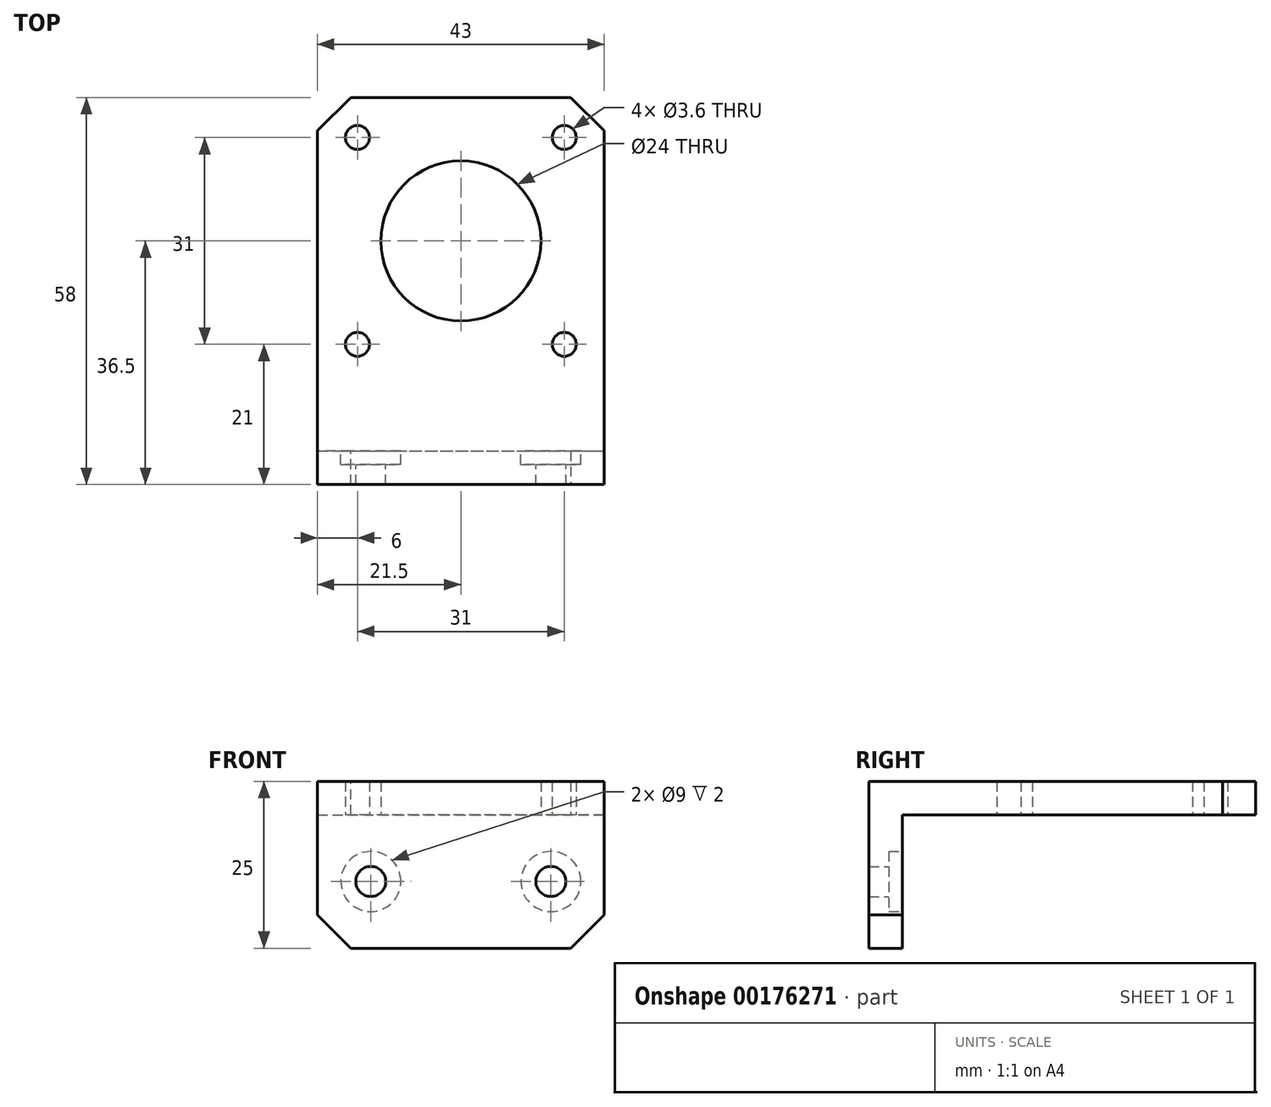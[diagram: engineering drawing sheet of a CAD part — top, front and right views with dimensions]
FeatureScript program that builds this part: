
annotation { "Feature Type Name" : "Feature", "Feature Type Description" : "" }
export const myFeature = defineFeature(function(context is Context, id is Id, definition is map)
    precondition{}
    {
        {
            var Q0;
            Q0=qCreatedBy(makeId("Top.planeOp"),FACE);
            var sketch = newSketch(context, id + "F0", { "sketchPlane" : qUnion([Q0])});
            skCircle(sketch, "E0", {"center": v(0, 0) * mm, "radius": 12 * mm});
            skLineSegment(sketch, "E1.bottom", {"start": v(15.5, -15.5) * mm, "end": v(-15.5, -15.5) * mm, "construction": true});
            skLineSegment(sketch, "E1.top", {"start": v(15.5, 15.5) * mm, "end": v(-15.5, 15.5) * mm, "construction": true});
            skLineSegment(sketch, "E1.left", {"start": v(15.5, -15.5) * mm, "end": v(15.5, 15.5) * mm, "construction": true});
            skLineSegment(sketch, "E1.right", {"start": v(-15.5, -15.5) * mm, "end": v(-15.5, 15.5) * mm, "construction": true});
            skCircle(sketch, "E2", {"center": v(15.5, 15.5) * mm, "radius": 1.8 * mm});
            skCircle(sketch, "E3", {"center": v(15.5, -15.5) * mm, "radius": 1.8 * mm});
            skCircle(sketch, "E4", {"center": v(-15.5, -15.5) * mm, "radius": 1.8 * mm});
            skCircle(sketch, "E5", {"center": v(-15.5, 15.5) * mm, "radius": 1.8 * mm});
            skLineSegment(sketch, "E6.bottom", {"start": v(21.5, -21.5) * mm, "end": v(-21.5, -21.5) * mm});
            skLineSegment(sketch, "E6.top", {"start": v(21.5, 21.5) * mm, "end": v(-21.5, 21.5) * mm});
            skLineSegment(sketch, "E6.left", {"start": v(21.5, -21.5) * mm, "end": v(21.5, 21.5) * mm});
            skLineSegment(sketch, "E6.right", {"start": v(-21.5, -21.5) * mm, "end": v(-21.5, 21.5) * mm});
            skLineSegment(sketch, "E7", {"start": v(-21.5, -21.5) * mm, "end": v(-21.5, -36.5) * mm});
            skLineSegment(sketch, "E8", {"start": v(-21.5, -36.5) * mm, "end": v(21.5, -36.5) * mm});
            skLineSegment(sketch, "E9", {"start": v(21.5, -36.5) * mm, "end": v(21.5, -21.5) * mm});
            skLineSegment(sketch, "E10", {"start": v(-21.5, -31.5) * mm, "end": v(21.5, -31.5) * mm});
            skSolve(sketch);
        }
        {
            var Q0;
            Q0=makeQuery(id+"F0.imprint","IMPRINT",FACE,{"disambiguationData":[TD([[makeQuery(id+"F0.imprint","IMPRINT",EDGE,{"derivedFrom":sQuery(id+"F0.wireOp",EDGE,"E0")}),-1.0]])]});
            var Q1;
            {var subQ0=sQuery(id+"F0.wireOp",EDGE,"E6.bottom");Q1=makeQuery(id+"F0.imprint","IMPRINT",FACE,{"disambiguationData":[TD([[makeQuery(id+"F0.imprint","IMPRINT",EDGE,{"derivedFrom":subQ0}),1.0]])]});}
            extrude(context, id + "F1", {"entities" : qUnion([Q0, Q1]), "depth" : 5 * mm});
        }
        {
            var Q0;
            {var subQ0=sQuery(id+"F0.wireOp",EDGE,"E8");Q0=makeQuery(id+"F0.imprint","IMPRINT",FACE,{"disambiguationData":[TD([[makeQuery(id+"F0.imprint","IMPRINT",EDGE,{"derivedFrom":subQ0}),1.0]])]});}
            extrude(context, id + "F2", {"entities" : qUnion([Q0]), "operationType" : NewBodyOperationType.ADD, "depth" : 5 * mm, "hasSecondDirection" : true, "secondDirectionOppositeDirection" : true, "secondDirectionDepth" : 20 * mm});
        }
        {
            var Q0;
            Q0=makeQuery(id+"F2.opExtrude","SWEPT_FACE",FACE,{"disambiguationData":[OSD([sQuery(id+"F0.wireOp",EDGE,"E10")])]});
            var sketch = newSketch(context, id + "F3", { "sketchPlane" : qUnion([Q0])});
            skCircle(sketch, "E11", {"center": v(-13.5, -10) * mm, "radius": 2.25 * mm});
            skPoint(sketch, "E11.centerSnap0", {"position": v(-21.5, -10) * mm});
            skCircle(sketch, "E12", {"center": v(13.5, -10) * mm, "radius": 2.25 * mm});
            skCircle(sketch, "E13", {"center": v(-13.5, -10) * mm, "radius": 4.5 * mm});
            skCircle(sketch, "E14", {"center": v(13.5, -10) * mm, "radius": 4.5 * mm});
            skSolve(sketch);
        }
        {
            var Q0;
            Q0=makeQuery(id+"F3.imprint","IMPRINT",FACE,{"disambiguationData":[TD([[makeQuery(id+"F3.imprint","IMPRINT",EDGE,{"derivedFrom":sQuery(id+"F3.wireOp",EDGE,"E11")}),1.0]])]});
            var Q1;
            Q1=makeQuery(id+"F3.imprint","IMPRINT",FACE,{"disambiguationData":[TD([[makeQuery(id+"F3.imprint","IMPRINT",EDGE,{"derivedFrom":sQuery(id+"F3.wireOp",EDGE,"E12")}),1.0]])]});
            extrude(context, id + "F4", {"entities" : qUnion([Q0, Q1]), "operationType" : NewBodyOperationType.REMOVE, "endBound" : BoundingType.UP_TO_NEXT, "oppositeDirection" : true, "depth" : 25 * mm});
        }
        {
            var Q0;
            Q0=makeQuery(id+"F3.imprint","IMPRINT",FACE,{"disambiguationData":[TD([[makeQuery(id+"F3.imprint","IMPRINT",EDGE,{"derivedFrom":sQuery(id+"F3.wireOp",EDGE,"E11")}),-1.0]])]});
            var Q1;
            Q1=makeQuery(id+"F3.imprint","IMPRINT",FACE,{"disambiguationData":[TD([[makeQuery(id+"F3.imprint","IMPRINT",EDGE,{"derivedFrom":sQuery(id+"F3.wireOp",EDGE,"E12")}),-1.0]])]});
            extrude(context, id + "F5", {"entities" : qUnion([Q0, Q1]), "operationType" : NewBodyOperationType.REMOVE, "oppositeDirection" : true, "depth" : 2 * mm});
        }
        {
            var Q0;
            Q0=makeQuery(id+"F1.opExtrude","SWEPT_EDGE",EDGE,{"disambiguationData":[OSD([sQuery(id+"F0.wireOp",EDGE,"E6.top"),sQuery(id+"F0.wireOp",EDGE,"E6.right")])]});
            var Q1;
            Q1=makeQuery(id+"F1.opExtrude","SWEPT_EDGE",EDGE,{"disambiguationData":[OSD([sQuery(id+"F0.wireOp",EDGE,"E6.top"),sQuery(id+"F0.wireOp",EDGE,"E6.left")])]});
            var Q2;
            Q2=makeQuery(id+"F2.opExtrude","CAP_EDGE",EDGE,{"disambiguationData":[OSD([sQuery(id+"F0.wireOp",EDGE,"E7")])],"isStart":true});
            var Q3;
            Q3=makeQuery(id+"F2.opExtrude","CAP_EDGE",EDGE,{"disambiguationData":[OSD([sQuery(id+"F0.wireOp",EDGE,"E9")])],"isStart":true});
            var Q4;
            Q4=makeQuery(id+"F1.opExtrude","CAP_EDGE",EDGE,{"disambiguationData":[OSD([sQuery(id+"F0.wireOp",EDGE,"E10")])],"isStart":true});
            chamfer(context, id + "F6", {"entities" : qUnion([Q0, Q1, Q2, Q3, Q4]), "width" : 5 * mm, "tangentPropagation" : true});
        }
    });
